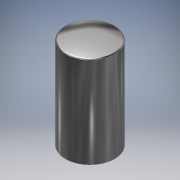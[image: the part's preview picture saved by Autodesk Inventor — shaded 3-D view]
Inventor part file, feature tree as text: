
AUTODESK INVENTOR PART (.ipt)
format: ipt  version: 2018 (Build 220112000, 112)  size: 127,488 bytes
history: native  units: in
note: dims shown in document units (in); Inventor stores cm internally (conversion verified against a paired STEP export)
features: revolve x1, fillet x1, sketch x1
ambient origin geometry x8: Origin, YZ Plane, XZ Plane, XY Plane, X Axis, Y Axis, Z Axis, Center Point
bodies: Solid1 (feature_tree)
feature tree (3):
  revolve  "Revolution1"  [1 undecoded]
  fillet  "Fillet1"  Radius=0.5in
  sketch  "Sketch1"  dims[d0=6.0in d2=0.5in d4=0.5in d5=6.0in d6=90.0deg d7=0.125in d8=2.5in]
note: 1 required parameter value undecoded (feature->parameter linkage not recoverable at this tier; creation-order binding heuristic only, values carry confidence <= 0.55)
